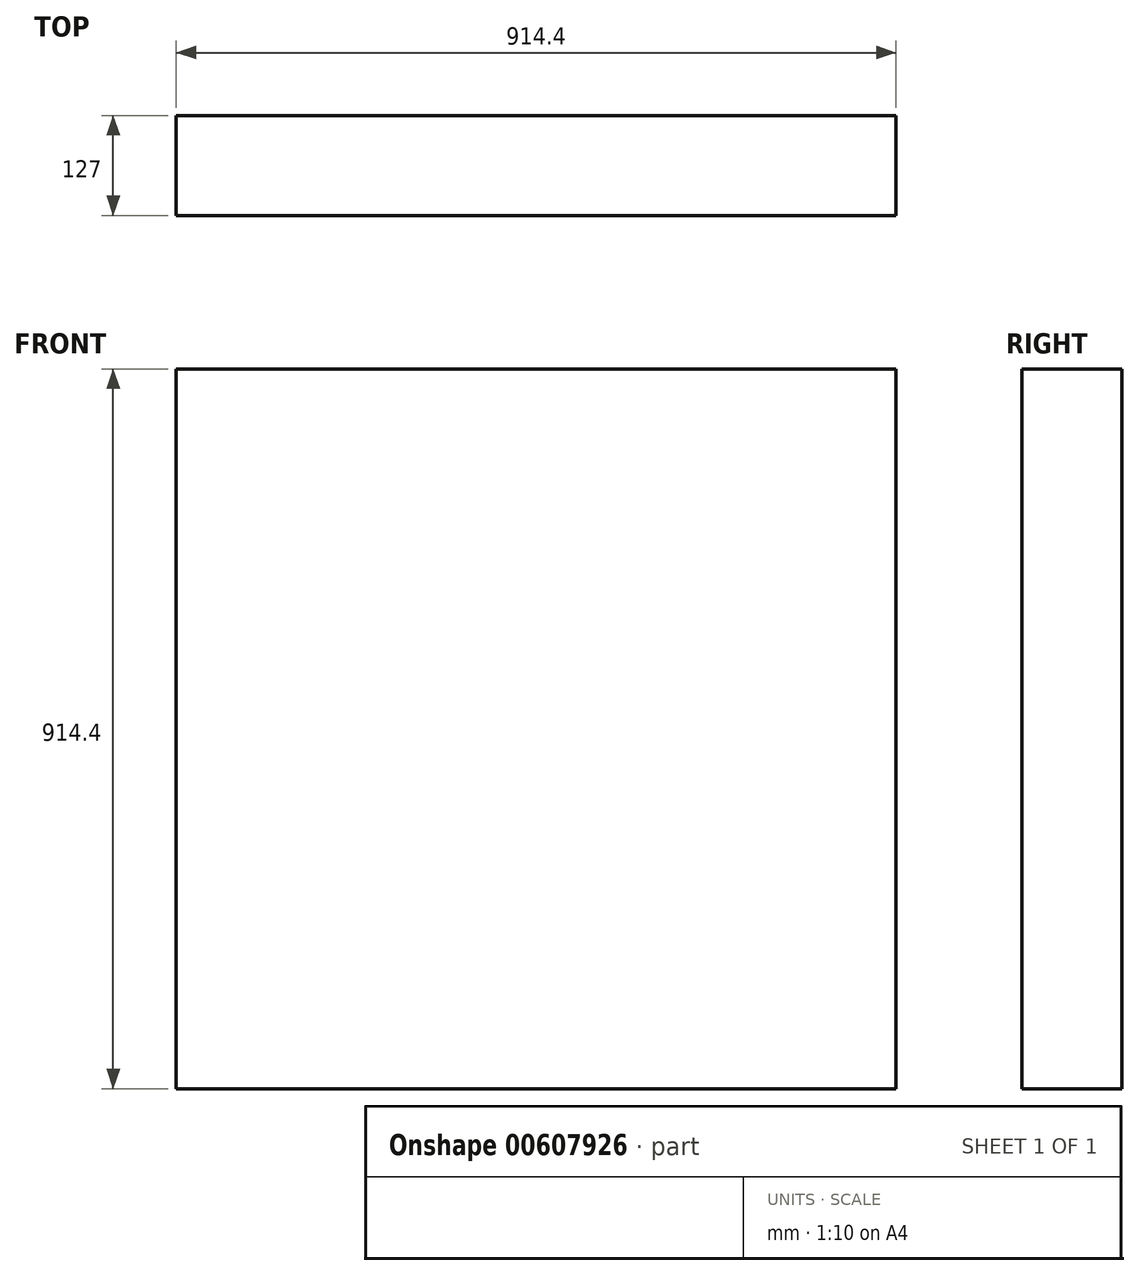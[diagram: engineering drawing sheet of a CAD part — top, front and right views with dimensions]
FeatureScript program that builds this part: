
annotation { "Feature Type Name" : "Feature", "Feature Type Description" : "" }
export const myFeature = defineFeature(function(context is Context, id is Id, definition is map)
    precondition{}
    {
        {
            var Q0;
            Q0=qCreatedBy(makeId("Front.planeOp"),FACE);
            var sketch = newSketch(context, id + "F0", { "sketchPlane" : qUnion([Q0])});
            skLineSegment(sketch, "E0.bottom", {"start": v(-457.2, 457.2) * mm, "end": v(457.2, 457.2) * mm});
            skLineSegment(sketch, "E0.top", {"start": v(-457.2, -457.2) * mm, "end": v(457.2, -457.2) * mm});
            skLineSegment(sketch, "E0.left", {"start": v(-457.2, 457.2) * mm, "end": v(-457.2, -457.2) * mm});
            skLineSegment(sketch, "E0.right", {"start": v(457.2, 457.2) * mm, "end": v(457.2, -457.2) * mm});
            skPoint(sketch, "E0.middle", {"position": v(0, 0) * mm});
            skSolve(sketch);
        }
        {
            var Q0;
            Q0=makeQuery(id+"F0.imprint","IMPRINT",FACE,{"disambiguationData":[TD([[makeQuery(id+"F0.imprint","IMPRINT",EDGE,{"derivedFrom":sQuery(id+"F0.wireOp",EDGE,"E0.bottom")}),-1.0]])]});
            extrude(context, id + "F1", {"entities" : qUnion([Q0]), "depth" : 127 * mm, "offsetDistance" : 25.4 * mm});
        }
    });
